FCSTD DOCUMENT  (FreeCAD 0.21R33771 (Git))
Label: jrobot-x-axis-assembly
License: All rights reserved
LicenseURL: http://en.wikipedia.org/wiki/All_rights_reserved
objects: App::Link×76, App::DocumentObjectGroup×3, PartDesign::CoordinateSystem×1, App::FeaturePython×1, Spreadsheet::Sheet×1, App::Part×1
note: 1 computed .brp shape members not serialized (recipe doc carries the construction recipe); baked Part::Feature solids carry a one-line shape summary decoded from their .brp
EXTERNAL_REF file=jrobot-x-axis-parts.FCStd obj=LCS_X_Axis_Base_Top
EXTERNAL_REF file=jrobot-x-axis-parts.FCStd obj=LCS_X_Axis_Top_Origin
EXTERNAL_REF file=jrobot-x-axis-parts.FCStd obj=Part
EXTERNAL_REF file=jrobot-x-axis-parts.FCStd obj=LCS_X_Axis_Top_Bearing_0
EXTERNAL_REF file=standard-parts.FCStd obj=LCS_Bearing_78mm_60mm_Bottom004
EXTERNAL_REF file=standard-parts.FCStd obj=Part006
EXTERNAL_REF file=jrobot-x-axis-parts.FCStd obj=LCS_X_Axis_Top_Bearing_1
EXTERNAL_REF file=standard-parts.FCStd obj=LCS_Bearing_78mm_60mm_Top004
EXTERNAL_REF file=jrobot-x-axis-parts.FCStd obj=LCS_X_Axis_Top_VerticalBearing_004
EXTERNAL_REF file=jrobot-x-axis-parts.FCStd obj=LCS_X_Axis_Top_VerticalBearing_2
EXTERNAL_REF file=jrobot-x-axis-parts.FCStd obj=LCS_X_Axis_Top_VerticalBearing_003
EXTERNAL_REF file=jrobot-x-axis-parts.FCStd obj=LCS_X_Axis_Top_VerticalBearing_3
EXTERNAL_REF file=jrobot-x-axis-parts.FCStd obj=LCS_X_Axis_Top_VerticalBearing_0
EXTERNAL_REF file=jrobot-x-axis-parts.FCStd obj=LCS_X_Axis_Top_LimitSwitch_0
EXTERNAL_REF file=standard-parts.FCStd obj=LCS_LimitSwitch_Hole0
EXTERNAL_REF file=standard-parts.FCStd obj=Part014
EXTERNAL_REF file=jrobot-x-axis-parts.FCStd obj=LCS_X_Axis_Base_BearingCap_To
EXTERNAL_REF file=jrobot-x-axis-parts.FCStd obj=Part018
EXTERNAL_REF file=jrobot-x-axis-parts.FCStd obj=LCS_X_Axis_Base_Origin
EXTERNAL_REF file=jrobot-x-axis-parts.FCStd obj=Part019
EXTERNAL_REF file=jrobot-x-axis-parts.FCStd obj=LCS_MotorMount_Origin
EXTERNAL_REF file=jrobot-x-axis-parts.FCStd obj=LCS_X_Axis_Top_MotorMount
EXTERNAL_REF file=jrobot-x-axis-parts.FCStd obj=Part020
EXTERNAL_REF file=jrobot-x-axis-parts.FCStd obj=LCS_X_Axis_MotorMount_Motor
EXTERNAL_REF file=standard-parts.FCStd obj=LCS_Nema23_76mm_MountFace
EXTERNAL_REF file=standard-parts.FCStd obj=Part015
EXTERNAL_REF file=jrobot-x-axis-parts.FCStd obj=LCS_X_Axis_Belt_Origin
EXTERNAL_REF file=jrobot-x-axis-parts.FCStd obj=LCS_X_Axis_Rotor_Belt
EXTERNAL_REF file=jrobot-x-axis-parts.FCStd obj=Part021
EXTERNAL_REF file=jrobot-x-axis-parts.FCStd obj=LCS_X_Axis_Rotor_Origin
EXTERNAL_REF file=jrobot-x-axis-parts.FCStd obj=LCS_X_Axis_Top_Rotor
EXTERNAL_REF file=jrobot-x-axis-parts.FCStd obj=Part022
EXTERNAL_REF file=jrobot-x-axis-parts.FCStd obj=LCS_X_Axis_BeltTensioner_Origin
EXTERNAL_REF file=jrobot-x-axis-parts.FCStd obj=LCS_X_Axis_MotorMount_Tensioner
EXTERNAL_REF file=jrobot-x-axis-parts.FCStd obj=Part023
EXTERNAL_REF file=jrobot-x-axis-parts.FCStd obj=LCS_X_Axis_BeltTensioner_Idler0
EXTERNAL_REF file=standard-parts.FCStd obj=LCS_Belt_Idler_GT2_10mm_Bottom
EXTERNAL_REF file=standard-parts.FCStd obj=Part009
EXTERNAL_REF file=jrobot-x-axis-parts.FCStd obj=LCS_X_Axis_BeltTensioner_Idler1
EXTERNAL_REF file=jrobot-x-axis-parts.FCStd obj=LCS_X_Axis_Shaft_Bottom
EXTERNAL_REF file=jrobot-x-axis-parts.FCStd obj=Part024
EXTERNAL_REF file=jrobot-x-axis-parts.FCStd obj=LCS_X_Axis_BeltTensioner_Bolt0
EXTERNAL_REF file=standard-parts.FCStd obj=LCS_M3_16_Screw
EXTERNAL_REF file=standard-parts.FCStd obj=Part020
EXTERNAL_REF file=jrobot-x-axis-parts.FCStd obj=LCS_X_Axis_BeltTensioner_Bolt1
EXTERNAL_REF file=standard-parts.FCStd obj=LCS_LimitSwitch_Hole0_Top
EXTERNAL_REF file=standard-parts.FCStd obj=LCS_M3_12_Screw
EXTERNAL_REF file=standard-parts.FCStd obj=Part018
EXTERNAL_REF file=standard-parts.FCStd obj=LCS_LimitSwitch_Hole1_Top
EXTERNAL_REF file=jrobot-x-axis-parts.FCStd obj=LCS_X_Axis_BeltTensioner_IdlerBolt0
EXTERNAL_REF file=standard-parts.FCStd obj=LCS_M5_25_Screw
EXTERNAL_REF file=standard-parts.FCStd obj=Part031
EXTERNAL_REF file=jrobot-x-axis-parts.FCStd obj=LCS_X_Axis_BeltTensioner_IdlerBolt1
EXTERNAL_REF file=standard-parts.FCStd obj=LCS_M3_Nut001
EXTERNAL_REF file=standard-parts.FCStd obj=Part037
EXTERNAL_REF file=standard-parts.FCStd obj=LCS_M5_20_Screw
EXTERNAL_REF file=standard-parts.FCStd obj=LCS_Nema23_76mm_Hole0
EXTERNAL_REF file=standard-parts.FCStd obj=Part030
EXTERNAL_REF file=standard-parts.FCStd obj=LCS_Nema23_76mm_Hole1
EXTERNAL_REF file=standard-parts.FCStd obj=LCS_Nema23_76mm_Hole2
EXTERNAL_REF file=standard-parts.FCStd obj=LCS_Nema23_76mm_Hole3
EXTERNAL_REF file=standard-parts.FCStd obj=LCS_Belt_Sprocket_GT2_6mm_5mm_Top001
EXTERNAL_REF file=standard-parts.FCStd obj=LCS_Nema23_76mm_Shaft
EXTERNAL_REF file=standard-parts.FCStd obj=Part038
EXTERNAL_REF file=jrobot-x-axis-parts.FCStd obj=LCS_X_Axis_Base_Bolt0
EXTERNAL_REF file=jrobot-x-axis-parts.FCStd obj=LCS_X_Axis_Base_Bolt1
EXTERNAL_REF file=jrobot-x-axis-parts.FCStd obj=LCS_X_Axis_Base_Bolt2
EXTERNAL_REF file=jrobot-x-axis-parts.FCStd obj=LCS_X_Axis_Base_Bolt3
EXTERNAL_REF file=jrobot-x-axis-parts.FCStd obj=LCS_X_Axis_Base_Bolt4
EXTERNAL_REF file=standard-parts.FCStd obj=LCS_M3_Nut
EXTERNAL_REF file=standard-parts.FCStd obj=Part024
EXTERNAL_REF file=jrobot-x-axis-parts.FCStd obj=LCS_X_Axis_Base_VerticalBearing_Bolt0
EXTERNAL_REF file=standard-parts.FCStd obj=LCS_M5_17_Screw
EXTERNAL_REF file=standard-parts.FCStd obj=Part029
EXTERNAL_REF file=jrobot-x-axis-parts.FCStd obj=LCS_X_Axis_Base_VerticalBearing_Bolt1
EXTERNAL_REF file=jrobot-x-axis-parts.FCStd obj=LCS_X_Axis_Base_VerticalBearing_Bolt2
EXTERNAL_REF file=jrobot-x-axis-parts.FCStd obj=LCS_X_Axis_Base_VerticalBearing_Bolt3
EXTERNAL_REF file=jrobot-x-axis-parts.FCStd obj=LCS_X_Axis_Base_VerticalBearing_Bolt4
EXTERNAL_REF file=jrobot-x-axis-parts.FCStd obj=LCS_X_Axis_Top_LimitSwitch_1
EXTERNAL_REF file=jrobot-x-axis-parts.FCStd obj=LCS_X_Axis_Base_Mount0
EXTERNAL_REF file=standard-parts.FCStd obj=LCS_M5_45_Screw001
EXTERNAL_REF file=standard-parts.FCStd obj=Part032
EXTERNAL_REF file=jrobot-x-axis-parts.FCStd obj=LCS_X_Axis_Base_Mount1
EXTERNAL_REF file=standard-parts.FCStd obj=LCS_M5_30_Screw
EXTERNAL_REF file=jrobot-x-axis-parts.FCStd obj=LCS_X_Axis_Base_Mount2
EXTERNAL_REF file=jrobot-x-axis-parts.FCStd obj=LCS_X_Axis_Base_Mount3
EXTERNAL_REF file=jrobot-x-axis-parts.FCStd obj=LCS_X_Axis_MotorMount_Mount0
EXTERNAL_REF file=jrobot-x-axis-parts.FCStd obj=LCS_X_Axis_MotorMount_Mount1
EXTERNAL_REF file=jrobot-x-axis-parts.FCStd obj=LCS_X_Axis_MotorMount_Mount2
EXTERNAL_REF file=jrobot-x-axis-parts.FCStd obj=LCS_X_Axis_MotorMount_Mount3

FEATURE [PartDesign::CoordinateSystem] LCS_Origin
  AttacherType = Attacher::AttachEngine3D
  MapMode = 2
  Support = -> [X_Axis]
FEATURE [App::DocumentObjectGroup] Constraints
FEATURE [App::FeaturePython] Variables  # WARN: FeaturePython — macro-defined, semantics opaque (R4)
  Type = App::PropertyContainer
FEATURE [App::DocumentObjectGroup] Configurations
FEATURE [App::Link] P_X_Axis_Top
  AttachedBy = #LCS_X_Axis_Top_Origin
  AttachedTo = P_X_Axis_Base#LCS_X_Axis_Base_Top
  LinkPlacement = pos=(0,0,42) rot=(0,0,1;0rad)
  LinkedObject = -> <external jrobot-x-axis-parts.FCStd>#Part
  Placement = pos=(0,0,42) rot=(0,0,1;0rad)
  SolverId = Asm4EE
  expr: Placement = P_X_Axis_Base.Placement * jrobot_x_axis_parts#LCS_X_Axis_Base_Top.Placement * AttachmentOffset * jrobot_x_axis_parts#LCS_X_Axis_Top_Origin.Placement ^ -1
FEATURE [App::Link] P_Bearing_5mm_16mm_5mm  label="P_Bearing_5mm_16mm_5mm_axis_bottom"
  AttachedBy = #LCS_Bearing_78mm_60mm_Bottom004
  AttachedTo = P_X_Axis_Top#LCS_X_Axis_Top_Bearing_0
  AttachmentOffset = pos=(0,0,0) rot=(1,0,0;3.14159rad)
  LinkPlacement = pos=(0,0,47) rot=(0.707107,0.707107,0;3.14159rad)
  LinkedObject = -> <external standard-parts.FCStd>#Part006
  Placement = pos=(0,0,47) rot=(0.707107,0.707107,0;3.14159rad)
  SolverId = Asm4EE
  expr: Placement = P_X_Axis_Top.Placement * jrobot_x_axis_parts#LCS_X_Axis_Top_Bearing_0.Placement * AttachmentOffset * standard_parts#LCS_Bearing_78mm_60mm_Bottom004.Placement ^ -1
FEATURE [App::Link] P_Bearing_5mm_16mm_5mm001  label="P_Bearing_5mm_16mm_5mm_axis_top"
  AttachedBy = #LCS_Bearing_78mm_60mm_Top004
  AttachedTo = P_X_Axis_Top#LCS_X_Axis_Top_Bearing_1
  AttachmentOffset = pos=(0,0,0) rot=(1,0,0;3.14159rad)
  LinkPlacement = pos=(-6e-16,0,82) rot=(0.707107,0.707107,0;3.14159rad)
  LinkedObject = -> <external standard-parts.FCStd>#Part006
  Placement = pos=(-6e-16,0,82) rot=(0.707107,0.707107,0;3.14159rad)
  SolverId = Asm4EE
  expr: Placement = P_X_Axis_Top.Placement * jrobot_x_axis_parts#LCS_X_Axis_Top_Bearing_1.Placement * AttachmentOffset * standard_parts#LCS_Bearing_78mm_60mm_Top004.Placement ^ -1
FEATURE [App::Link] P_Bearing_5mm_16mm_1  label="P_Bearing_5mm_16mm_radial_1"
  AttachedBy = #LCS_Bearing_78mm_60mm_Bottom004
  AttachedTo = P_X_Axis_Top#LCS_X_Axis_Top_VerticalBearing_004
  LinkPlacement = pos=(-77.5,2.49e-14,77) rot=(0.707107,0,-0.707107;3.14159rad)
  LinkedObject = -> <external standard-parts.FCStd>#Part006
  Placement = pos=(-77.5,2.49e-14,77) rot=(0.707107,0,-0.707107;3.14159rad)
  SolverId = Asm4EE
  expr: Placement = P_X_Axis_Top.Placement * jrobot_x_axis_parts#LCS_X_Axis_Top_VerticalBearing_004.Placement * AttachmentOffset * standard_parts#LCS_Bearing_78mm_60mm_Bottom004.Placement ^ -1
FEATURE [App::Link] P_Bearing_5mm_16mm_2  label="P_Bearing_5mm_16mm_radial_2"
  AttachedBy = #LCS_Bearing_78mm_60mm_Bottom004
  AttachedTo = P_X_Axis_Top#LCS_X_Axis_Top_VerticalBearing_2
  LinkPlacement = pos=(-23.9488,-73.7069,77) rot=(0.62896,0.456966,-0.62896;2.28433rad)
  LinkedObject = -> <external standard-parts.FCStd>#Part006
  Placement = pos=(-23.9488,-73.7069,77) rot=(0.62896,0.456966,-0.62896;2.28433rad)
  SolverId = Asm4EE
  expr: Placement = P_X_Axis_Top.Placement * jrobot_x_axis_parts#LCS_X_Axis_Top_VerticalBearing_2.Placement * AttachmentOffset * standard_parts#LCS_Bearing_78mm_60mm_Bottom004.Placement ^ -1
FEATURE [App::Link] P_Bearing_5mm_16mm_3  label="P_Bearing_5mm_16mm_radial_3"
  AttachedBy = #LCS_Bearing_78mm_60mm_Bottom004
  AttachedTo = P_X_Axis_Top#LCS_X_Axis_Top_VerticalBearing_003
  LinkPlacement = pos=(62.6988,-45.5534,77) rot=(0.295242,0.908661,-0.295242;1.66643rad)
  LinkedObject = -> <external standard-parts.FCStd>#Part006
  Placement = pos=(62.6988,-45.5534,77) rot=(0.295242,0.908661,-0.295242;1.66643rad)
  SolverId = Asm4EE
  expr: Placement = P_X_Axis_Top.Placement * jrobot_x_axis_parts#LCS_X_Axis_Top_VerticalBearing_003.Placement * AttachmentOffset * standard_parts#LCS_Bearing_78mm_60mm_Bottom004.Placement ^ -1
FEATURE [App::Link] P_Bearing_5mm_16mm_4  label="P_Bearing_5mm_16mm_radial_4"
  AttachedBy = #LCS_Bearing_78mm_60mm_Bottom004
  AttachedTo = P_X_Axis_Top#LCS_X_Axis_Top_VerticalBearing_3
  LinkPlacement = pos=(62.6988,45.5534,77) rot=(-0.295242,0.908661,0.295242;1.66643rad)
  LinkedObject = -> <external standard-parts.FCStd>#Part006
  Placement = pos=(62.6988,45.5534,77) rot=(-0.295242,0.908661,0.295242;1.66643rad)
  SolverId = Asm4EE
  expr: Placement = P_X_Axis_Top.Placement * jrobot_x_axis_parts#LCS_X_Axis_Top_VerticalBearing_3.Placement * AttachmentOffset * standard_parts#LCS_Bearing_78mm_60mm_Bottom004.Placement ^ -1
FEATURE [App::Link] P_Bearing_5mm_16mm_5mm002  label="P_Bearing_5mm_16mm_radial_0"
  AttachedBy = #LCS_Bearing_78mm_60mm_Bottom004
  AttachedTo = P_X_Axis_Top#LCS_X_Axis_Top_VerticalBearing_0
  LinkPlacement = pos=(-23.9488,73.7069,77) rot=(0.111299,-0.702714,-0.702714;2.91991rad)
  LinkedObject = -> <external standard-parts.FCStd>#Part006
  Placement = pos=(-23.9488,73.7069,77) rot=(0.111299,-0.702714,-0.702714;2.91991rad)
  SolverId = Asm4EE
  expr: Placement = P_X_Axis_Top.Placement * jrobot_x_axis_parts#LCS_X_Axis_Top_VerticalBearing_0.Placement * AttachmentOffset * standard_parts#LCS_Bearing_78mm_60mm_Bottom004.Placement ^ -1
FEATURE [App::Link] P_LimitSwitch
  AttachedBy = #LCS_LimitSwitch_Hole0
  AttachedTo = P_X_Axis_Top#LCS_X_Axis_Top_LimitSwitch_0
  AttachmentOffset = pos=(0,0,0) rot=(0,0,-1;3.14159rad)
  LinkPlacement = pos=(6.875,55.8,82) rot=(0,0,-1;3.14159rad)
  LinkedObject = -> <external standard-parts.FCStd>#Part014
  Placement = pos=(6.875,55.8,82) rot=(0,0,-1;3.14159rad)
  SolverId = Asm4EE
  expr: Placement = P_X_Axis_Top.Placement * jrobot_x_axis_parts#LCS_X_Axis_Top_LimitSwitch_0.Placement * AttachmentOffset * standard_parts#LCS_LimitSwitch_Hole0.Placement ^ -1
FEATURE [App::Link] P_Robot_X_Axis_Base_BearingCap
  AttachedBy = #LCS_X_Axis_Base_BearingCap_To
  AttachedTo = P_X_Axis_Top#LCS_X_Axis_Top_Origin
  LinkPlacement = pos=(0,0,40) rot=(0,0,1;0rad)
  LinkedObject = -> <external jrobot-x-axis-parts.FCStd>#Part018
  Placement = pos=(0,0,40) rot=(0,0,1;0rad)
  SolverId = Asm4EE
  expr: Placement = P_X_Axis_Top.Placement * jrobot_x_axis_parts#LCS_X_Axis_Top_Origin.Placement * AttachmentOffset * jrobot_x_axis_parts#LCS_X_Axis_Base_BearingCap_To.Placement ^ -1
FEATURE [App::Link] P_X_Axis_Base
  AttachedBy = #LCS_X_Axis_Base_Origin
  AttachedTo = Parent Assembly#LCS_Origin
  LinkedObject = -> <external jrobot-x-axis-parts.FCStd>#Part019
  SolverId = Asm4EE
  expr: Placement = LCS_Origin.Placement * AttachmentOffset * jrobot_x_axis_parts#LCS_X_Axis_Base_Origin.Placement ^ -1
FEATURE [App::Link] P_X_Axis_MotorMount
  AttachedBy = #LCS_MotorMount_Origin
  AttachedTo = P_X_Axis_Top#LCS_X_Axis_Top_MotorMount
  AttachmentOffset = pos=(0,0,0) rot=(0,0,1;3.14159rad)
  LinkPlacement = pos=(-1.1e-14,0,80) rot=(0,0,1;3.14159rad)
  LinkedObject = -> <external jrobot-x-axis-parts.FCStd>#Part020
  Placement = pos=(-1.1e-14,0,80) rot=(0,0,1;3.14159rad)
  SolverId = Asm4EE
  expr: Placement = P_X_Axis_Top.Placement * jrobot_x_axis_parts#LCS_X_Axis_Top_MotorMount.Placement * AttachmentOffset * jrobot_x_axis_parts#LCS_MotorMount_Origin.Placement ^ -1
FEATURE [App::Link] P_Nema23_76mm
  AttachedBy = #LCS_Nema23_76mm_MountFace
  AttachedTo = P_X_Axis_MotorMount#LCS_X_Axis_MotorMount_Motor
  LinkPlacement = pos=(4.1e-15,123.5,2) rot=(0,0,1;3.14159rad)
  LinkedObject = -> <external standard-parts.FCStd>#Part015
  Placement = pos=(4.1e-15,123.5,2) rot=(0,0,1;3.14159rad)
  SolverId = Asm4EE
  expr: Placement = P_X_Axis_MotorMount.Placement * jrobot_x_axis_parts#LCS_X_Axis_MotorMount_Motor.Placement * AttachmentOffset * standard_parts#LCS_Nema23_76mm_MountFace.Placement ^ -1
FEATURE [App::Link] P_X_Axis_Belt
  AttachedBy = #LCS_X_Axis_Belt_Origin
  AttachedTo = P_X_Axis_Rotor#LCS_X_Axis_Rotor_Belt
  LinkPlacement = pos=(0,0,87) rot=(0,0,1;0rad)
  LinkedObject = -> <external jrobot-x-axis-parts.FCStd>#Part021
  Placement = pos=(0,0,87) rot=(0,0,1;0rad)
  SolverId = Asm4EE
  expr: Placement = P_X_Axis_Rotor.Placement * jrobot_x_axis_parts#LCS_X_Axis_Rotor_Belt.Placement * AttachmentOffset * jrobot_x_axis_parts#LCS_X_Axis_Belt_Origin.Placement ^ -1
FEATURE [App::Link] P_X_Axis_Rotor
  AttachedBy = #LCS_X_Axis_Rotor_Origin
  AttachedTo = P_X_Axis_Top#LCS_X_Axis_Top_Rotor
  LinkPlacement = pos=(0,0,85) rot=(0,0,1;0rad)
  LinkedObject = -> <external jrobot-x-axis-parts.FCStd>#Part022
  Placement = pos=(0,0,85) rot=(0,0,1;0rad)
  SolverId = Asm4EE
  expr: Placement = P_X_Axis_Top.Placement * jrobot_x_axis_parts#LCS_X_Axis_Top_Rotor.Placement * AttachmentOffset * jrobot_x_axis_parts#LCS_X_Axis_Rotor_Origin.Placement ^ -1
FEATURE [App::Link] P_X_Axis_BeltTensioner
  AttachedBy = #LCS_X_Axis_BeltTensioner_Origin
  AttachedTo = P_X_Axis_MotorMount#LCS_X_Axis_MotorMount_Tensioner
  LinkPlacement = pos=(4.1e-15,123.5,85) rot=(0,0,1;3.14159rad)
  LinkedObject = -> <external jrobot-x-axis-parts.FCStd>#Part023
  Placement = pos=(4.1e-15,123.5,85) rot=(0,0,1;3.14159rad)
  SolverId = Asm4EE
  expr: Placement = P_X_Axis_MotorMount.Placement * jrobot_x_axis_parts#LCS_X_Axis_MotorMount_Tensioner.Placement * AttachmentOffset * jrobot_x_axis_parts#LCS_X_Axis_BeltTensioner_Origin.Placement ^ -1
FEATURE [App::Link] P_Belt_Idler_GT2_10mm_5mm
  AttachedBy = #LCS_Belt_Idler_GT2_10mm_Bottom
  AttachedTo = P_X_Axis_BeltTensioner#LCS_X_Axis_BeltTensioner_Idler0
  AttachmentOffset = pos=(0,0,1) rot=(0,0,1;0rad)
  LinkPlacement = pos=(15,116,98.5) rot=(-0.707107,0.707107,0;3.14159rad)
  LinkedObject = -> <external standard-parts.FCStd>#Part009
  Placement = pos=(15,116,98.5) rot=(-0.707107,0.707107,0;3.14159rad)
  SolverId = Asm4EE
  expr: Placement = P_X_Axis_BeltTensioner.Placement * jrobot_x_axis_parts#LCS_X_Axis_BeltTensioner_Idler0.Placement * AttachmentOffset * standard_parts#LCS_Belt_Idler_GT2_10mm_Bottom.Placement ^ -1
FEATURE [App::Link] P_Belt_Idler_GT2_10mm_5mm_2
  AttachedBy = #LCS_Belt_Idler_GT2_10mm_Bottom
  AttachedTo = P_X_Axis_BeltTensioner#LCS_X_Axis_BeltTensioner_Idler1
  AttachmentOffset = pos=(0,0,1) rot=(0,0,1;0rad)
  LinkPlacement = pos=(-15,116,98.5) rot=(-0.707107,0.707107,0;3.14159rad)
  LinkedObject = -> <external standard-parts.FCStd>#Part009
  Placement = pos=(-15,116,98.5) rot=(-0.707107,0.707107,0;3.14159rad)
  SolverId = Asm4EE
  expr: Placement = P_X_Axis_BeltTensioner.Placement * jrobot_x_axis_parts#LCS_X_Axis_BeltTensioner_Idler1.Placement * AttachmentOffset * standard_parts#LCS_Belt_Idler_GT2_10mm_Bottom.Placement ^ -1
FEATURE [App::Link] P_X_Axis_Shaft
  AttachedBy = #LCS_X_Axis_Shaft_Bottom
  AttachedTo = P_Robot_X_Axis_Base_BearingCap#LCS_X_Axis_Base_BearingCap_To
  LinkPlacement = pos=(0,0,42) rot=(0,0,1;0rad)
  LinkedObject = -> <external jrobot-x-axis-parts.FCStd>#Part024
  Placement = pos=(0,0,42) rot=(0,0,1;0rad)
  SolverId = Asm4EE
  expr: Placement = P_Robot_X_Axis_Base_BearingCap.Placement * jrobot_x_axis_parts#LCS_X_Axis_Base_BearingCap_To.Placement * AttachmentOffset * jrobot_x_axis_parts#LCS_X_Axis_Shaft_Bottom.Placement ^ -1
FEATURE [App::Link] P_M3_16_Screw  label="P_X_Axis_BeltTensioner_Bolt0_Bolt"
  AttachedBy = #LCS_M3_16_Screw
  AttachedTo = P_X_Axis_BeltTensioner#LCS_X_Axis_BeltTensioner_Bolt0
  LinkPlacement = pos=(42.5,123.5,83) rot=(0,0,1;4.71239rad)
  LinkedObject = -> <external standard-parts.FCStd>#Part020
  Placement = pos=(42.5,123.5,83) rot=(0,0,1;4.71239rad)
  SolverId = Asm4EE
  expr: Placement = P_X_Axis_BeltTensioner.Placement * jrobot_x_axis_parts#LCS_X_Axis_BeltTensioner_Bolt0.Placement * AttachmentOffset * standard_parts#LCS_M3_16_Screw.Placement ^ -1
FEATURE [App::Link] X_Axis_BeltTensioner_Bolt0_Screw  label="P_X_Axis_BeltTensioner_Bolt1_Bolt"
  AttachedBy = #LCS_M3_16_Screw
  AttachedTo = P_X_Axis_BeltTensioner#LCS_X_Axis_BeltTensioner_Bolt1
  LinkPlacement = pos=(-42.5,123.5,83) rot=(0,0,1;4.71239rad)
  LinkedObject = -> <external standard-parts.FCStd>#Part020
  Placement = pos=(-42.5,123.5,83) rot=(0,0,1;4.71239rad)
  SolverId = Asm4EE
  expr: Placement = P_X_Axis_BeltTensioner.Placement * jrobot_x_axis_parts#LCS_X_Axis_BeltTensioner_Bolt1.Placement * AttachmentOffset * standard_parts#LCS_M3_16_Screw.Placement ^ -1
FEATURE [App::Link] P_M3_12_Screw  label="P_X_Axis_LimitSwitch_Hole0_Bolt"
  AttachedBy = #LCS_M3_12_Screw
  AttachedTo = P_LimitSwitch#LCS_LimitSwitch_Hole0_Top
  LinkPlacement = pos=(9.625,50,84) rot=(0,0,-1;1.5708rad)
  LinkedObject = -> <external standard-parts.FCStd>#Part018
  Placement = pos=(9.625,50,84) rot=(0,0,-1;1.5708rad)
  SolverId = Asm4EE
  expr: Placement = P_LimitSwitch.Placement * standard_parts#LCS_LimitSwitch_Hole0_Top.Placement * AttachmentOffset * standard_parts#LCS_M3_12_Screw.Placement ^ -1
FEATURE [App::Link] P_M3_12_Screw_2  label="P_X_Axis_LimitSwitch_Hole1_Bolt"
  AttachedBy = #LCS_M3_12_Screw
  AttachedTo = P_LimitSwitch#LCS_LimitSwitch_Hole1_Top
  LinkPlacement = pos=(-9.625,50,84) rot=(0,0,-1;1.5708rad)
  LinkedObject = -> <external standard-parts.FCStd>#Part018
  Placement = pos=(-9.625,50,84) rot=(0,0,-1;1.5708rad)
  SolverId = Asm4EE
  expr: Placement = P_LimitSwitch.Placement * standard_parts#LCS_LimitSwitch_Hole1_Top.Placement * AttachmentOffset * standard_parts#LCS_M3_12_Screw.Placement ^ -1
FEATURE [App::Link] P_M5_25_Screw  label="P_X_Axis_BeltTensioner_IdlerBolt0_Bolt"
  AttachedBy = #LCS_M5_25_Screw
  AttachedTo = P_X_Axis_BeltTensioner#LCS_X_Axis_BeltTensioner_IdlerBolt0
  LinkPlacement = pos=(15,116,111) rot=(0,0,1;4.71239rad)
  LinkedObject = -> <external standard-parts.FCStd>#Part031
  Placement = pos=(15,116,111) rot=(0,0,1;4.71239rad)
  SolverId = Asm4EE
  expr: Placement = P_X_Axis_BeltTensioner.Placement * jrobot_x_axis_parts#LCS_X_Axis_BeltTensioner_IdlerBolt0.Placement * AttachmentOffset * standard_parts#LCS_M5_25_Screw.Placement ^ -1
FEATURE [App::Link] P_M5_25_Screw_2  label="P_X_Axis_BeltTensioner_IdlerBolt1_Bolt"
  AttachedBy = #LCS_M5_25_Screw
  AttachedTo = P_X_Axis_BeltTensioner#LCS_X_Axis_BeltTensioner_IdlerBolt1
  LinkPlacement = pos=(-15,116,111) rot=(0,0,1;4.71239rad)
  LinkedObject = -> <external standard-parts.FCStd>#Part031
  Placement = pos=(-15,116,111) rot=(0,0,1;4.71239rad)
  SolverId = Asm4EE
  expr: Placement = P_X_Axis_BeltTensioner.Placement * jrobot_x_axis_parts#LCS_X_Axis_BeltTensioner_IdlerBolt1.Placement * AttachmentOffset * standard_parts#LCS_M5_25_Screw.Placement ^ -1
FEATURE [App::Link] P_M5_Nut  label="P_X_Axis_BeltTensioner_IdlerBolt0_Nut"
  AttachedBy = #LCS_M3_Nut001
  AttachedTo = P_X_Axis_BeltTensioner#LCS_X_Axis_BeltTensioner_IdlerBolt0
  AttachmentOffset = pos=(0,0,-9.5) rot=(0,0,1;0rad)
  LinkPlacement = pos=(15,116,101.5) rot=(0,0,1;4.71239rad)
  LinkedObject = -> <external standard-parts.FCStd>#Part037
  Placement = pos=(15,116,101.5) rot=(0,0,1;4.71239rad)
  SolverId = Asm4EE
  expr: Placement = P_X_Axis_BeltTensioner.Placement * jrobot_x_axis_parts#LCS_X_Axis_BeltTensioner_IdlerBolt0.Placement * AttachmentOffset * standard_parts#LCS_M3_Nut001.Placement ^ -1
FEATURE [App::Link] P_M5_Nut001  label="P_X_Axis_BeltTensioner_IdlerBolt1_Nut"
  AttachedBy = #LCS_M3_Nut001
  AttachedTo = P_X_Axis_BeltTensioner#LCS_X_Axis_BeltTensioner_IdlerBolt1
  AttachmentOffset = pos=(0,0,-9.5) rot=(0,0,1;0rad)
  LinkPlacement = pos=(-15,116,101.5) rot=(0,0,1;4.71239rad)
  LinkedObject = -> <external standard-parts.FCStd>#Part037
  Placement = pos=(-15,116,101.5) rot=(0,0,1;4.71239rad)
  SolverId = Asm4EE
  expr: Placement = P_X_Axis_BeltTensioner.Placement * jrobot_x_axis_parts#LCS_X_Axis_BeltTensioner_IdlerBolt1.Placement * AttachmentOffset * standard_parts#LCS_M3_Nut001.Placement ^ -1
FEATURE [App::Link] P_M5_20_Screw  label="P_X_Axis_Nema17_Bolt0_Bolt"
  AttachedBy = #LCS_M5_20_Screw
  AttachedTo = P_Nema23_76mm#LCS_Nema23_76mm_Hole0
  AttachmentOffset = pos=(0,0,2) rot=(0,0,1;0rad)
  LinkPlacement = pos=(-23.5,100,80) rot=(0,0,1;3.14159rad)
  LinkedObject = -> <external standard-parts.FCStd>#Part030
  Placement = pos=(-23.5,100,80) rot=(0,0,1;3.14159rad)
  SolverId = Asm4EE
  expr: Placement = P_Nema23_76mm.Placement * standard_parts#LCS_Nema23_76mm_Hole0.Placement * AttachmentOffset * standard_parts#LCS_M5_20_Screw.Placement ^ -1
FEATURE [App::Link] P_M5_20_Screw001  label="P_X_Axis_Nema17_Bolt1_Bolt"
  AttachedBy = #LCS_M5_20_Screw
  AttachedTo = P_Nema23_76mm#LCS_Nema23_76mm_Hole1
  AttachmentOffset = pos=(0,0,2) rot=(0,0,1;0rad)
  LinkPlacement = pos=(23.5,100,80) rot=(0,0,1;3.14159rad)
  LinkedObject = -> <external standard-parts.FCStd>#Part030
  Placement = pos=(23.5,100,80) rot=(0,0,1;3.14159rad)
  SolverId = Asm4EE
  expr: Placement = P_Nema23_76mm.Placement * standard_parts#LCS_Nema23_76mm_Hole1.Placement * AttachmentOffset * standard_parts#LCS_M5_20_Screw.Placement ^ -1
FEATURE [App::Link] P_X_Axis_Nema17_Bolt1_Screw  label="P_X_Axis_Nema17_Bolt2_Bolt"
  AttachedBy = #LCS_M5_20_Screw
  AttachedTo = P_Nema23_76mm#LCS_Nema23_76mm_Hole2
  AttachmentOffset = pos=(0,0,2) rot=(0,0,1;0rad)
  LinkPlacement = pos=(-23.5,147,80) rot=(0,0,1;3.14159rad)
  LinkedObject = -> <external standard-parts.FCStd>#Part030
  Placement = pos=(-23.5,147,80) rot=(0,0,1;3.14159rad)
  SolverId = Asm4EE
  expr: Placement = P_Nema23_76mm.Placement * standard_parts#LCS_Nema23_76mm_Hole2.Placement * AttachmentOffset * standard_parts#LCS_M5_20_Screw.Placement ^ -1
FEATURE [App::Link] P_X_Axis_Nema17_Bolt1_1  label="P_X_Axis_Nema17_Bolt3_Bolt"
  AttachedBy = #LCS_M5_20_Screw
  AttachedTo = P_Nema23_76mm#LCS_Nema23_76mm_Hole3
  AttachmentOffset = pos=(0,0,2) rot=(0,0,1;0rad)
  LinkPlacement = pos=(23.5,147,80) rot=(0,0,1;3.14159rad)
  LinkedObject = -> <external standard-parts.FCStd>#Part030
  Placement = pos=(23.5,147,80) rot=(0,0,1;3.14159rad)
  SolverId = Asm4EE
  expr: Placement = P_Nema23_76mm.Placement * standard_parts#LCS_Nema23_76mm_Hole3.Placement * AttachmentOffset * standard_parts#LCS_M5_20_Screw.Placement ^ -1
FEATURE [App::Link] P_M5_Nut002  label="P_X_Axis_Nema17_Nut0"
  AttachedBy = #LCS_M3_Nut001
  AttachedTo = P_Nema23_76mm#LCS_Nema23_76mm_Hole0
  AttachmentOffset = pos=(0,0,-10) rot=(0,0,1;0rad)
  LinkPlacement = pos=(-23.5,100,68) rot=(0,0,1;3.14159rad)
  LinkedObject = -> <external standard-parts.FCStd>#Part037
  Placement = pos=(-23.5,100,68) rot=(0,0,1;3.14159rad)
  SolverId = Asm4EE
  expr: Placement = P_Nema23_76mm.Placement * standard_parts#LCS_Nema23_76mm_Hole0.Placement * AttachmentOffset * standard_parts#LCS_M3_Nut001.Placement ^ -1
FEATURE [App::Link] P_M5_Nut_2  label="P_X_Axis_Nema17_Nut1"
  AttachedBy = #LCS_M3_Nut001
  AttachedTo = P_Nema23_76mm#LCS_Nema23_76mm_Hole1
  AttachmentOffset = pos=(0,0,-10) rot=(0,0,1;0rad)
  LinkPlacement = pos=(23.5,100,68) rot=(0,0,1;3.14159rad)
  LinkedObject = -> <external standard-parts.FCStd>#Part037
  Placement = pos=(23.5,100,68) rot=(0,0,1;3.14159rad)
  SolverId = Asm4EE
  expr: Placement = P_Nema23_76mm.Placement * standard_parts#LCS_Nema23_76mm_Hole1.Placement * AttachmentOffset * standard_parts#LCS_M3_Nut001.Placement ^ -1
FEATURE [App::Link] P_M5_Nut_1  label="P_X_Axis_Nema17_Nut2"
  AttachedBy = #LCS_M3_Nut001
  AttachedTo = P_Nema23_76mm#LCS_Nema23_76mm_Hole2
  AttachmentOffset = pos=(0,0,-10) rot=(0,0,1;0rad)
  LinkPlacement = pos=(-23.5,147,68) rot=(0,0,1;3.14159rad)
  LinkedObject = -> <external standard-parts.FCStd>#Part037
  Placement = pos=(-23.5,147,68) rot=(0,0,1;3.14159rad)
  SolverId = Asm4EE
  expr: Placement = P_Nema23_76mm.Placement * standard_parts#LCS_Nema23_76mm_Hole2.Placement * AttachmentOffset * standard_parts#LCS_M3_Nut001.Placement ^ -1
FEATURE [App::Link] P_M5_Nut003  label="P_X_Axis_Nema17_Nut3"
  AttachedBy = #LCS_M3_Nut001
  AttachedTo = P_Nema23_76mm#LCS_Nema23_76mm_Hole3
  AttachmentOffset = pos=(0,0,-10) rot=(0,0,1;0rad)
  LinkPlacement = pos=(23.5,147,68) rot=(0,0,1;3.14159rad)
  LinkedObject = -> <external standard-parts.FCStd>#Part037
  Placement = pos=(23.5,147,68) rot=(0,0,1;3.14159rad)
  SolverId = Asm4EE
  expr: Placement = P_Nema23_76mm.Placement * standard_parts#LCS_Nema23_76mm_Hole3.Placement * AttachmentOffset * standard_parts#LCS_M3_Nut001.Placement ^ -1
FEATURE [App::Link] P_Belt_Sprocket_GT2_6mm_10mm
  AttachedBy = #LCS_Belt_Sprocket_GT2_6mm_5mm_Top001
  AttachedTo = P_Nema23_76mm#LCS_Nema23_76mm_Shaft
  LinkPlacement = pos=(4.1e-15,123.5,86) rot=(0,0,1;3.14159rad)
  LinkedObject = -> <external standard-parts.FCStd>#Part038
  Placement = pos=(4.1e-15,123.5,86) rot=(0,0,1;3.14159rad)
  SolverId = Asm4EE
  expr: Placement = P_Nema23_76mm.Placement * standard_parts#LCS_Nema23_76mm_Shaft.Placement * AttachmentOffset * standard_parts#LCS_Belt_Sprocket_GT2_6mm_5mm_Top001.Placement ^ -1
FEATURE [Spreadsheet::Sheet] BOM
  cells = A1='BomKey; B1='DrawingName; C1='DrawingRevision; D1='PartID; E1='PartDescription; F1='FileName; G1='FastenerDiameter; H1='FastenerLength; I1='FastenerType; J1='Qty.; A2='jrobot_x_axis_assembly#Assembly; B2='jrobot-x-axis-assembly.FCStd; D2='jrobot-x-axis-assembly; G2='-; H2='-; I2='-; J2=1; A3='jrobot_x_axis_parts#Part; B3='jrobot-x-axis-parts.FCStd; D3='jrobot-x-axis-parts; E3='B_X_Axis_Top; G3='-; H3='-; I3='-; J3=1; A4='standard_parts#Part006; B4='standard-parts.FCStd; D4='standard-parts; E4='B_Bearing_5mm_16mm_5mm; G4='-; H4='-; I4='-; J4=7; A5='jrobot_x_axis_parts#Part019; B5='jrobot-x-axis-parts.FCStd; D5='jrobot-x-axis-parts; E5='B_X_Axis_Base; G5='-; H5='-; I5='-; J5=1; A6='jrobot_x_axis_parts#Part018; B6='jrobot-x-axis-parts.FCStd; D6='jrobot-x-axis-parts; E6='B_X_Axis_BearingCap; G6='-; H6='-; I6='-; J6=1; A7='standard_parts#Part014; B7='standard-parts.FCStd; D7='standard-parts; E7='B_LimitSwitch; G7='-; H7='-; I7='-; J7=1; A8='jrobot_x_axis_parts#Part020; B8='jrobot-x-axis-parts.FCStd; D8='jrobot-x-axis-parts; E8='B_X_Axis_MotorMount; G8='-; H8='-; I8='-; J8=1; A9='standard_parts#Part015; B9='standard-parts.FCStd; D9='standard-parts; E9='B_Nema23_76mm; G9='-; H9='-; I9='-; J9=1; A10='jrobot_x_axis_parts#Part021; B10='jrobot-x-axis-parts.FCStd; D10='jrobot-x-axis-parts; E10='B_X_Axis_Belt; G10='-; H10='-; I10='-; J10=1; A11='jrobot_x_axis_parts#Part022; B11='jrobot-x-axis-parts.FCStd; D11='jrobot-x-axis-parts; E11='B_X_Axis_Rotor; G11='-; H11='-; I11='-; J11=1; A12='jrobot_x_axis_parts#Part023; B12='jrobot-x-axis-parts.FCStd; D12='jrobot-x-axis-parts; E12='B_X_Axis_BeltTensioner; G12='-; H12='-; I12='-; J12=1; A13='standard_parts#Part009; B13='standard-parts.FCStd; D13='standard-parts; E13='B_Belt_Idler_GT2_10mm_5mm; G13='-; H13='-; I13='-; J13=2; A14='jrobot_x_axis_parts#Part024; B14='jrobot-x-axis-parts.FCStd; D14='jrobot-x-axis-parts; E14='B_X_Axis_Shaft; G14='-; H14='-; I14='-; J14=1; A15='standard_parts#Part020; B15='standard-parts.FCStd; D15='standard-parts; E15='B_M3_16_Screw; G15='-; H15='-; I15='-; J15=2; A16='M3x16-Screw(ISO4762); B16='All; C16='-; D16='M3x16-Screw(ISO4762); E16='-; F16='-; G16='M3; H16=16; I16='ISO4762; J16=2; A17='standard_parts#Part018; B17='standard-parts.FCStd; C17='a; D17='standard-parts; E17='B_M3_12_Screw; F17='a; G17='-; H17='-; I17='-; J17=2; A18='M3x12-Screw(ISO4762); B18='All; C18='-; D18='M3x12-Screw(ISO4762); E18='-; F18='-; G18='M3; H18=12; I18='ISO4762; J18=2; A19='standard_parts#Part031; B19='standard-parts.FCStd; D19='standard-parts; E19='B_M5_25_Screw; G19='-; H19='-; I19='-; J19=2; A20='M5x25-Screw(ISO4762); B20='All; C20='-; D20='M5x25-Screw(ISO4762); E20='-; F20='-; G20='M5; H20=25; I20='ISO4762; J20=2; A21='standard_parts#Part037; B21='standard-parts.FCStd; D21='standard-parts; E21='B_M5_Nut; G21='-; H21='-; I21='-; J21=6; A22='M5-Nut(ISO4032); B22='All; C22='-; D22='M5-Nut(ISO4032); E22='-; F22='-; G22='M5; I22='ISO4032; J22=6; A23='standard_parts#Part030; B23='standard-parts.FCStd; D23='standard-parts; E23='B_M5_20_Screw; G23='-; H23='-; I23='-; J23=4; A24='M5x20-Screw(ISO4762); B24='All; C24='-; D24='M5x20-Screw(ISO4762); E24='-; F24='-; +12 more cells
FEATURE [App::Link] P_M3_12_Screw001  label="P_X_Axis_Overlap_Bolt0_Bolt"
  AttachedBy = #LCS_M3_12_Screw
  AttachedTo = P_X_Axis_Base#LCS_X_Axis_Base_Bolt0
  LinkPlacement = pos=(52.8818,-72.7856,46.9994) rot=(0.90714,0.294748,0.300368;1.64928rad)
  LinkedObject = -> <external standard-parts.FCStd>#Part018
  Placement = pos=(52.8818,-72.7856,46.9994) rot=(0.90714,0.294748,0.300368;1.64928rad)
  SolverId = Asm4EE
  expr: Placement = P_X_Axis_Base.Placement * jrobot_x_axis_parts#LCS_X_Axis_Base_Bolt0.Placement * AttachmentOffset * standard_parts#LCS_M3_12_Screw.Placement ^ -1
FEATURE [App::Link] P_M3_X_Axis_Overlap_1  label="P_X_Axis_Overlap_Bolt1_Bolt"
  AttachedBy = #LCS_M3_12_Screw
  AttachedTo = P_X_Axis_Base#LCS_X_Axis_Base_Bolt1
  LinkPlacement = pos=(85.5646,27.8016,46.9994) rot=(0.453526,0.624225,0.636128;2.27573rad)
  LinkedObject = -> <external standard-parts.FCStd>#Part018
  Placement = pos=(85.5646,27.8016,46.9994) rot=(0.453526,0.624225,0.636128;2.27573rad)
  SolverId = Asm4EE
  expr: Placement = P_X_Axis_Base.Placement * jrobot_x_axis_parts#LCS_X_Axis_Base_Bolt1.Placement * AttachmentOffset * standard_parts#LCS_M3_12_Screw.Placement ^ -1
FEATURE [App::Link] P_M3_X_Axis_Overlap_2  label="P_X_Axis_Overlap_Bolt2_Bolt"
  AttachedBy = #LCS_M3_12_Screw
  AttachedTo = P_X_Axis_Base#LCS_X_Axis_Base_Bolt2
  LinkPlacement = pos=(-6.64599e-08,89.9679,46.9994) rot=(0,0.700397,0.713753;3.14159rad)
  LinkedObject = -> <external standard-parts.FCStd>#Part018
  Placement = pos=(-6.64599e-08,89.9679,46.9994) rot=(0,0.700397,0.713753;3.14159rad)
  SolverId = Asm4EE
  expr: Placement = P_X_Axis_Base.Placement * jrobot_x_axis_parts#LCS_X_Axis_Base_Bolt2.Placement * AttachmentOffset * standard_parts#LCS_M3_12_Screw.Placement ^ -1
FEATURE [App::Link] P_M3_X_Axis_Overlap_3  label="P_X_Axis_Overlap_Bolt3_Bolt"
  AttachedBy = #LCS_M3_12_Screw
  AttachedTo = P_X_Axis_Base#LCS_X_Axis_Base_Bolt3
  LinkPlacement = pos=(-85.5646,27.8016,46.9994) rot=(-0.453526,0.624224,0.636128;4.00746rad)
  LinkedObject = -> <external standard-parts.FCStd>#Part018
  Placement = pos=(-85.5646,27.8016,46.9994) rot=(-0.453526,0.624224,0.636128;4.00746rad)
  SolverId = Asm4EE
  expr: Placement = P_X_Axis_Base.Placement * jrobot_x_axis_parts#LCS_X_Axis_Base_Bolt3.Placement * AttachmentOffset * standard_parts#LCS_M3_12_Screw.Placement ^ -1
FEATURE [App::Link] P_M3_X_Axis_Overlap_4  label="P_X_Axis_Overlap_Bolt4_Bolt"
  AttachedBy = #LCS_M3_12_Screw
  AttachedTo = P_X_Axis_Base#LCS_X_Axis_Base_Bolt4
  LinkPlacement = pos=(-52.8818,-72.7856,46.9994) rot=(0.90714,-0.294748,-0.300368;1.64928rad)
  LinkedObject = -> <external standard-parts.FCStd>#Part018
  Placement = pos=(-52.8818,-72.7856,46.9994) rot=(0.90714,-0.294748,-0.300368;1.64928rad)
  SolverId = Asm4EE
  expr: Placement = P_X_Axis_Base.Placement * jrobot_x_axis_parts#LCS_X_Axis_Base_Bolt4.Placement * AttachmentOffset * standard_parts#LCS_M3_12_Screw.Placement ^ -1
FEATURE [App::Link] P_M3_Nut  label="P_X_Axis_Overlap_Bolt0_Nut"
  AttachedBy = #LCS_M3_Nut
  AttachedTo = P_X_Axis_Base#LCS_X_Axis_Base_Bolt0
  AttachmentOffset = pos=(0,0,-8) rot=(0,0,1;0rad)
  LinkPlacement = pos=(48.1804,-66.3146,46.8483) rot=(0.90714,0.294748,0.300368;1.64928rad)
  LinkedObject = -> <external standard-parts.FCStd>#Part024
  Placement = pos=(48.1804,-66.3146,46.8483) rot=(0.90714,0.294748,0.300368;1.64928rad)
  SolverId = Asm4EE
  expr: Placement = P_X_Axis_Base.Placement * jrobot_x_axis_parts#LCS_X_Axis_Base_Bolt0.Placement * AttachmentOffset * standard_parts#LCS_M3_Nut.Placement ^ -1
FEATURE [App::Link] P_M3_X_Axis_Overlap_5  label="P_X_Axis_Overlap_Bolt1_Nut"
  AttachedBy = #LCS_M3_Nut
  AttachedTo = P_X_Axis_Base#LCS_X_Axis_Base_Bolt1
  AttachmentOffset = pos=(0,0,-8) rot=(0,0,1;0rad)
  LinkPlacement = pos=(77.9575,25.3299,46.8483) rot=(0.453526,0.624225,0.636128;2.27573rad)
  LinkedObject = -> <external standard-parts.FCStd>#Part024
  Placement = pos=(77.9575,25.3299,46.8483) rot=(0.453526,0.624225,0.636128;2.27573rad)
  SolverId = Asm4EE
  expr: Placement = P_X_Axis_Base.Placement * jrobot_x_axis_parts#LCS_X_Axis_Base_Bolt1.Placement * AttachmentOffset * standard_parts#LCS_M3_Nut.Placement ^ -1
FEATURE [App::Link] P_M3_X_Axis_Overlap_6  label="P_X_Axis_Overlap_Bolt2_Nut"
  AttachedBy = #LCS_M3_Nut
  AttachedTo = P_X_Axis_Base#LCS_X_Axis_Base_Bolt2
  AttachmentOffset = pos=(0,0,-8) rot=(0,0,1;0rad)
  LinkPlacement = pos=(2.55178e-07,81.9693,46.8483) rot=(0,0.700397,0.713753;3.14159rad)
  LinkedObject = -> <external standard-parts.FCStd>#Part024
  Placement = pos=(2.55178e-07,81.9693,46.8483) rot=(0,0.700397,0.713753;3.14159rad)
  SolverId = Asm4EE
  expr: Placement = P_X_Axis_Base.Placement * jrobot_x_axis_parts#LCS_X_Axis_Base_Bolt2.Placement * AttachmentOffset * standard_parts#LCS_M3_Nut.Placement ^ -1
FEATURE [App::Link] P_M3_X_Axis_Overlap_7  label="P_X_Axis_Overlap_Bolt3_Nut"
  AttachedBy = #LCS_M3_Nut
  AttachedTo = P_X_Axis_Base#LCS_X_Axis_Base_Bolt3
  AttachmentOffset = pos=(0,0,-8) rot=(0,0,1;0rad)
  LinkPlacement = pos=(-77.9575,25.3299,46.8483) rot=(-0.453526,0.624224,0.636128;4.00746rad)
  LinkedObject = -> <external standard-parts.FCStd>#Part024
  Placement = pos=(-77.9575,25.3299,46.8483) rot=(-0.453526,0.624224,0.636128;4.00746rad)
  SolverId = Asm4EE
  expr: Placement = P_X_Axis_Base.Placement * jrobot_x_axis_parts#LCS_X_Axis_Base_Bolt3.Placement * AttachmentOffset * standard_parts#LCS_M3_Nut.Placement ^ -1
FEATURE [App::Link] P_M3_X_Axis_Overlap_8  label="P_X_Axis_Overlap_Bolt4_Nut"
  AttachedBy = #LCS_M3_Nut
  AttachedTo = P_X_Axis_Base#LCS_X_Axis_Base_Bolt4
  AttachmentOffset = pos=(0,0,-8) rot=(0,0,1;0rad)
  LinkPlacement = pos=(-48.1804,-66.3146,46.8483) rot=(0.90714,-0.294748,-0.300368;1.64928rad)
  LinkedObject = -> <external standard-parts.FCStd>#Part024
  Placement = pos=(-48.1804,-66.3146,46.8483) rot=(0.90714,-0.294748,-0.300368;1.64928rad)
  SolverId = Asm4EE
  expr: Placement = P_X_Axis_Base.Placement * jrobot_x_axis_parts#LCS_X_Axis_Base_Bolt4.Placement * AttachmentOffset * standard_parts#LCS_M3_Nut.Placement ^ -1
FEATURE [App::Link] P_M5_20_Screw002  label="P_X_Axis_Base_VerticalBearing_Bolt0_Bolt"
  AttachedBy = #LCS_M5_17_Screw
  AttachedTo = P_X_Axis_Top#LCS_X_Axis_Base_VerticalBearing_Bolt0
  LinkPlacement = pos=(-26.2664,80.8398,77) rot=(0.62896,-0.456966,-0.62896;3.99886rad)
  LinkedObject = -> <external standard-parts.FCStd>#Part029
  Placement = pos=(-26.2664,80.8398,77) rot=(0.62896,-0.456966,-0.62896;3.99886rad)
  SolverId = Asm4EE
  expr: Placement = P_X_Axis_Top.Placement * jrobot_x_axis_parts#LCS_X_Axis_Base_VerticalBearing_Bolt0.Placement * AttachmentOffset * standard_parts#LCS_M5_17_Screw.Placement ^ -1
FEATURE [App::Link] P_M5_16_Screw  label="P_X_Axis_Base_VerticalBearing_Bolt1_Bolt"
  AttachedBy = #LCS_M5_17_Screw
  AttachedTo = P_X_Axis_Top#LCS_X_Axis_Base_VerticalBearing_Bolt1
  LinkPlacement = pos=(-85,2.66e-14,77) rot=(0.707107,0,-0.707107;3.14159rad)
  LinkedObject = -> <external standard-parts.FCStd>#Part029
  Placement = pos=(-85,2.66e-14,77) rot=(0.707107,0,-0.707107;3.14159rad)
  SolverId = Asm4EE
  expr: Placement = P_X_Axis_Top.Placement * jrobot_x_axis_parts#LCS_X_Axis_Base_VerticalBearing_Bolt1.Placement * AttachmentOffset * standard_parts#LCS_M5_17_Screw.Placement ^ -1
FEATURE [App::Link] P_M5_16_Screw_2  label="P_X_Axis_Base_VerticalBearing_Bolt2_Bolt"
  AttachedBy = #LCS_M5_17_Screw
  AttachedTo = P_X_Axis_Top#LCS_X_Axis_Base_VerticalBearing_Bolt2
  LinkPlacement = pos=(-26.2664,-80.8398,77) rot=(0.62896,0.456966,-0.62896;2.28433rad)
  LinkedObject = -> <external standard-parts.FCStd>#Part029
  Placement = pos=(-26.2664,-80.8398,77) rot=(0.62896,0.456966,-0.62896;2.28433rad)
  SolverId = Asm4EE
  expr: Placement = P_X_Axis_Top.Placement * jrobot_x_axis_parts#LCS_X_Axis_Base_VerticalBearing_Bolt2.Placement * AttachmentOffset * standard_parts#LCS_M5_17_Screw.Placement ^ -1
FEATURE [App::Link] P_M5_16_Screw_1  label="P_X_Axis_Base_VerticalBearing_Bolt3_Bolt"
  AttachedBy = #LCS_M5_17_Screw
  AttachedTo = P_X_Axis_Top#LCS_X_Axis_Base_VerticalBearing_Bolt3
  LinkPlacement = pos=(68.7664,-49.9617,77) rot=(0.295242,0.908661,-0.295242;1.66643rad)
  LinkedObject = -> <external standard-parts.FCStd>#Part029
  Placement = pos=(68.7664,-49.9617,77) rot=(0.295242,0.908661,-0.295242;1.66643rad)
  SolverId = Asm4EE
  expr: Placement = P_X_Axis_Top.Placement * jrobot_x_axis_parts#LCS_X_Axis_Base_VerticalBearing_Bolt3.Placement * AttachmentOffset * standard_parts#LCS_M5_17_Screw.Placement ^ -1
FEATURE [App::Link] P_M5_16_Screw_3  label="P_X_Axis_Base_VerticalBearing_Bolt4_Bolt"
  AttachedBy = #LCS_M5_17_Screw
  AttachedTo = P_X_Axis_Top#LCS_X_Axis_Base_VerticalBearing_Bolt4
  LinkPlacement = pos=(68.7664,49.9617,77) rot=(-0.295242,0.908661,0.295242;1.66643rad)
  LinkedObject = -> <external standard-parts.FCStd>#Part029
  Placement = pos=(68.7664,49.9617,77) rot=(-0.295242,0.908661,0.295242;1.66643rad)
  SolverId = Asm4EE
  expr: Placement = P_X_Axis_Top.Placement * jrobot_x_axis_parts#LCS_X_Axis_Base_VerticalBearing_Bolt4.Placement * AttachmentOffset * standard_parts#LCS_M5_17_Screw.Placement ^ -1
FEATURE [App::Link] P_M5_Nut004  label="P_X_Axis_Base_VerticalBearing_Bolt0_Nut"
  AttachedBy = #LCS_M3_Nut001
  AttachedTo = P_X_Axis_Top#LCS_X_Axis_Base_VerticalBearing_Bolt0
  AttachmentOffset = pos=(0,0,-13) rot=(0,0,1;0rad)
  LinkPlacement = pos=(-22.2492,68.4761,77) rot=(0.62896,-0.456966,-0.62896;3.99886rad)
  LinkedObject = -> <external standard-parts.FCStd>#Part037
  Placement = pos=(-22.2492,68.4761,77) rot=(0.62896,-0.456966,-0.62896;3.99886rad)
  SolverId = Asm4EE
  expr: Placement = P_X_Axis_Top.Placement * jrobot_x_axis_parts#LCS_X_Axis_Base_VerticalBearing_Bolt0.Placement * AttachmentOffset * standard_parts#LCS_M3_Nut001.Placement ^ -1
FEATURE [App::Link] P_M5_Nut_3  label="P_X_Axis_Base_VerticalBearing_Bolt1_Nut"
  AttachedBy = #LCS_M3_Nut001
  AttachedTo = P_X_Axis_Top#LCS_X_Axis_Base_VerticalBearing_Bolt1
  AttachmentOffset = pos=(0,0,-13) rot=(0,0,1;0rad)
  LinkPlacement = pos=(-72,2.38e-14,77) rot=(0.707107,0,-0.707107;3.14159rad)
  LinkedObject = -> <external standard-parts.FCStd>#Part037
  Placement = pos=(-72,2.38e-14,77) rot=(0.707107,0,-0.707107;3.14159rad)
  SolverId = Asm4EE
  expr: Placement = P_X_Axis_Top.Placement * jrobot_x_axis_parts#LCS_X_Axis_Base_VerticalBearing_Bolt1.Placement * AttachmentOffset * standard_parts#LCS_M3_Nut001.Placement ^ -1
FEATURE [App::Link] P_M5_Nut_4  label="P_X_Axis_Base_VerticalBearing_Bolt2_Nut"
  AttachedBy = #LCS_M3_Nut001
  AttachedTo = P_X_Axis_Top#LCS_X_Axis_Base_VerticalBearing_Bolt2
  AttachmentOffset = pos=(0,0,-13) rot=(0,0,1;0rad)
  LinkPlacement = pos=(-22.2492,-68.4761,77) rot=(0.62896,0.456966,-0.62896;2.28433rad)
  LinkedObject = -> <external standard-parts.FCStd>#Part037
  Placement = pos=(-22.2492,-68.4761,77) rot=(0.62896,0.456966,-0.62896;2.28433rad)
  SolverId = Asm4EE
  expr: Placement = P_X_Axis_Top.Placement * jrobot_x_axis_parts#LCS_X_Axis_Base_VerticalBearing_Bolt2.Placement * AttachmentOffset * standard_parts#LCS_M3_Nut001.Placement ^ -1
FEATURE [App::Link] P_M5_Nut_5  label="P_X_Axis_Base_VerticalBearing_Bolt3_Nut"
  AttachedBy = #LCS_M3_Nut001
  AttachedTo = P_X_Axis_Top#LCS_X_Axis_Base_VerticalBearing_Bolt3
  AttachmentOffset = pos=(0,0,-13) rot=(0,0,1;0rad)
  LinkPlacement = pos=(58.2492,-42.3205,77) rot=(0.295242,0.908661,-0.295242;1.66643rad)
  LinkedObject = -> <external standard-parts.FCStd>#Part037
  Placement = pos=(58.2492,-42.3205,77) rot=(0.295242,0.908661,-0.295242;1.66643rad)
  SolverId = Asm4EE
  expr: Placement = P_X_Axis_Top.Placement * jrobot_x_axis_parts#LCS_X_Axis_Base_VerticalBearing_Bolt3.Placement * AttachmentOffset * standard_parts#LCS_M3_Nut001.Placement ^ -1
FEATURE [App::Link] P_M5_Nut_6  label="P_X_Axis_Base_VerticalBearing_Bolt4_Nut"
  AttachedBy = #LCS_M3_Nut001
  AttachedTo = P_X_Axis_Top#LCS_X_Axis_Base_VerticalBearing_Bolt4
  AttachmentOffset = pos=(0,0,-13) rot=(0,0,1;0rad)
  LinkPlacement = pos=(58.2492,42.3205,77) rot=(-0.295242,0.908661,0.295242;1.66643rad)
  LinkedObject = -> <external standard-parts.FCStd>#Part037
  Placement = pos=(58.2492,42.3205,77) rot=(-0.295242,0.908661,0.295242;1.66643rad)
  SolverId = Asm4EE
  expr: Placement = P_X_Axis_Top.Placement * jrobot_x_axis_parts#LCS_X_Axis_Base_VerticalBearing_Bolt4.Placement * AttachmentOffset * standard_parts#LCS_M3_Nut001.Placement ^ -1
FEATURE [App::Link] P_M3_Nut001  label="P_X_Axis_LimitSwitch_Hole0_Nut"
  AttachedBy = #LCS_M3_Nut
  AttachedTo = P_X_Axis_Top#LCS_X_Axis_Top_LimitSwitch_0
  AttachmentOffset = pos=(0,0,-7) rot=(0,0,1;0rad)
  LinkPlacement = pos=(9.625,50,75) rot=(0,0,1;1.5708rad)
  LinkedObject = -> <external standard-parts.FCStd>#Part024
  Placement = pos=(9.625,50,75) rot=(0,0,1;1.5708rad)
  SolverId = Asm4EE
  expr: Placement = P_X_Axis_Top.Placement * jrobot_x_axis_parts#LCS_X_Axis_Top_LimitSwitch_0.Placement * AttachmentOffset * standard_parts#LCS_M3_Nut.Placement ^ -1
FEATURE [App::Link] P_M3_Nut_2  label="P_X_Axis_LimitSwitch_Hole1_Nut"
  AttachedBy = #LCS_M3_Nut
  AttachedTo = P_X_Axis_Top#LCS_X_Axis_Top_LimitSwitch_1
  AttachmentOffset = pos=(0,0,-7) rot=(0,0,1;0rad)
  LinkPlacement = pos=(-9.625,50,75) rot=(0,0,1;1.5708rad)
  LinkedObject = -> <external standard-parts.FCStd>#Part024
  Placement = pos=(-9.625,50,75) rot=(0,0,1;1.5708rad)
  SolverId = Asm4EE
  expr: Placement = P_X_Axis_Top.Placement * jrobot_x_axis_parts#LCS_X_Axis_Top_LimitSwitch_1.Placement * AttachmentOffset * standard_parts#LCS_M3_Nut.Placement ^ -1
FEATURE [App::Link] P_M5_50_Screw  label="P_M5_X_Axis_Base_Mount_Bolt0"
  AttachedBy = #LCS_M5_45_Screw001
  AttachedTo = P_X_Axis_Base#LCS_X_Axis_Base_Mount0
  LinkPlacement = pos=(-75,-75,5) rot=(0,0,1;1.5708rad)
  LinkedObject = -> <external standard-parts.FCStd>#Part032
  Placement = pos=(-75,-75,5) rot=(0,0,1;1.5708rad)
  SolverId = Asm4EE
  expr: Placement = P_X_Axis_Base.Placement * jrobot_x_axis_parts#LCS_X_Axis_Base_Mount0.Placement * AttachmentOffset * standard_parts#LCS_M5_45_Screw001.Placement ^ -1
FEATURE [App::Link] P_M5_50_Screw_2  label="P_M5_X_Axis_Base_Mount_Bolt1"
  AttachedBy = #LCS_M5_30_Screw
  AttachedTo = P_X_Axis_Base#LCS_X_Axis_Base_Mount1
  LinkPlacement = pos=(75,-75,5) rot=(0,0,-1;1.5708rad)
  LinkedObject = -> <external standard-parts.FCStd>#Part032
  Placement = pos=(75,-75,5) rot=(0,0,-1;1.5708rad)
  SolverId = Asm4EE
  expr: Placement = P_X_Axis_Base.Placement * jrobot_x_axis_parts#LCS_X_Axis_Base_Mount1.Placement * AttachmentOffset * standard_parts#LCS_M5_30_Screw.Placement ^ -1
FEATURE [App::Link] P_M5_50_Screw_1  label="P_M5_X_Axis_Base_Mount_Bolt2"
  AttachedBy = #LCS_M5_30_Screw
  AttachedTo = P_X_Axis_Base#LCS_X_Axis_Base_Mount2
  LinkPlacement = pos=(75,75,5) rot=(0,0,-1;1.5708rad)
  LinkedObject = -> <external standard-parts.FCStd>#Part032
  Placement = pos=(75,75,5) rot=(0,0,-1;1.5708rad)
  SolverId = Asm4EE
  expr: Placement = P_X_Axis_Base.Placement * jrobot_x_axis_parts#LCS_X_Axis_Base_Mount2.Placement * AttachmentOffset * standard_parts#LCS_M5_30_Screw.Placement ^ -1
FEATURE [App::Link] P_M5_50_Screw_3  label="P_M5_X_Axis_Base_Mount_Bolt3"
  AttachedBy = #LCS_M5_30_Screw
  AttachedTo = P_X_Axis_Base#LCS_X_Axis_Base_Mount3
  LinkPlacement = pos=(-75,75,5) rot=(0,0,1;1.5708rad)
  LinkedObject = -> <external standard-parts.FCStd>#Part032
  Placement = pos=(-75,75,5) rot=(0,0,1;1.5708rad)
  SolverId = Asm4EE
  expr: Placement = P_X_Axis_Base.Placement * jrobot_x_axis_parts#LCS_X_Axis_Base_Mount3.Placement * AttachmentOffset * standard_parts#LCS_M5_30_Screw.Placement ^ -1
FEATURE [App::Link] P_M5_Nut005  label="P_M5_X_Axis_Base_Mount_Nut0"
  AttachedBy = #LCS_M3_Nut001
  AttachedTo = P_X_Axis_Base#LCS_X_Axis_Base_Mount0
  AttachmentOffset = pos=(0,0,-20) rot=(0,0,1;0rad)
  LinkPlacement = pos=(-75,-75,-15) rot=(0,0,1;1.5708rad)
  LinkedObject = -> <external standard-parts.FCStd>#Part037
  Placement = pos=(-75,-75,-15) rot=(0,0,1;1.5708rad)
  SolverId = Asm4EE
  expr: Placement = P_X_Axis_Base.Placement * jrobot_x_axis_parts#LCS_X_Axis_Base_Mount0.Placement * AttachmentOffset * standard_parts#LCS_M3_Nut001.Placement ^ -1
FEATURE [App::Link] P_M5_Nut_7  label="P_M5_X_Axis_Base_Mount_Nut1"
  AttachedBy = #LCS_M3_Nut001
  AttachedTo = P_X_Axis_Base#LCS_X_Axis_Base_Mount1
  AttachmentOffset = pos=(0,0,-20) rot=(0,0,1;0rad)
  LinkPlacement = pos=(75,-75,-15) rot=(0,0,-1;1.5708rad)
  LinkedObject = -> <external standard-parts.FCStd>#Part037
  Placement = pos=(75,-75,-15) rot=(0,0,-1;1.5708rad)
  SolverId = Asm4EE
  expr: Placement = P_X_Axis_Base.Placement * jrobot_x_axis_parts#LCS_X_Axis_Base_Mount1.Placement * AttachmentOffset * standard_parts#LCS_M3_Nut001.Placement ^ -1
FEATURE [App::Link] P_M5_Nut_8  label="P_M5_X_Axis_Base_Mount_Nut2"
  AttachedBy = #LCS_M3_Nut001
  AttachedTo = P_X_Axis_Base#LCS_X_Axis_Base_Mount2
  AttachmentOffset = pos=(0,0,-20) rot=(0,0,1;0rad)
  LinkPlacement = pos=(75,75,-15) rot=(0,0,-1;1.5708rad)
  LinkedObject = -> <external standard-parts.FCStd>#Part037
  Placement = pos=(75,75,-15) rot=(0,0,-1;1.5708rad)
  SolverId = Asm4EE
  expr: Placement = P_X_Axis_Base.Placement * jrobot_x_axis_parts#LCS_X_Axis_Base_Mount2.Placement * AttachmentOffset * standard_parts#LCS_M3_Nut001.Placement ^ -1
FEATURE [App::Link] P_M5_Nut_9  label="P_M5_X_Axis_Base_Mount_Nut3"
  AttachedBy = #LCS_M3_Nut001
  AttachedTo = P_X_Axis_Base#LCS_X_Axis_Base_Mount3
  AttachmentOffset = pos=(0,0,-20) rot=(0,0,1;0rad)
  LinkPlacement = pos=(-75,75,-15) rot=(0,0,1;1.5708rad)
  LinkedObject = -> <external standard-parts.FCStd>#Part037
  Placement = pos=(-75,75,-15) rot=(0,0,1;1.5708rad)
  SolverId = Asm4EE
  expr: Placement = P_X_Axis_Base.Placement * jrobot_x_axis_parts#LCS_X_Axis_Base_Mount3.Placement * AttachmentOffset * standard_parts#LCS_M3_Nut001.Placement ^ -1
FEATURE [App::Link] P_M3_12_Screw002  label="P_M3_X_Axis_MotorMount_Bolt0"
  AttachedBy = #LCS_M3_12_Screw
  AttachedTo = P_X_Axis_MotorMount#LCS_X_Axis_MotorMount_Mount0
  LinkPlacement = pos=(62.2084,69.0894,72.0005) rot=(-0.88065,0.33805,-0.331931;1.71565rad)
  LinkedObject = -> <external standard-parts.FCStd>#Part020
  Placement = pos=(62.2084,69.0894,72.0005) rot=(-0.88065,0.33805,-0.331931;1.71565rad)
  SolverId = Asm4EE
  expr: Placement = P_X_Axis_MotorMount.Placement * jrobot_x_axis_parts#LCS_X_Axis_MotorMount_Mount0.Placement * AttachmentOffset * standard_parts#LCS_M3_12_Screw.Placement ^ -1
FEATURE [App::Link] P_M3_12_Screw_3  label="P_M3_X_Axis_MotorMount_Bolt1"
  AttachedBy = #LCS_M3_16_Screw
  AttachedTo = P_X_Axis_MotorMount#LCS_X_Axis_MotorMount_Mount1
  LinkPlacement = pos=(62.2084,69.0894,62.0005) rot=(-0.88065,0.33805,-0.331931;1.71565rad)
  LinkedObject = -> <external standard-parts.FCStd>#Part020
  Placement = pos=(62.2084,69.0894,62.0005) rot=(-0.88065,0.33805,-0.331931;1.71565rad)
  SolverId = Asm4EE
  expr: Placement = P_X_Axis_MotorMount.Placement * jrobot_x_axis_parts#LCS_X_Axis_MotorMount_Mount1.Placement * AttachmentOffset * standard_parts#LCS_M3_16_Screw.Placement ^ -1
FEATURE [App::Link] P_M3_12_Screw_1  label="P_M3_X_Axis_MotorMount_Bolt2"
  AttachedBy = #LCS_M3_16_Screw
  AttachedTo = P_X_Axis_MotorMount#LCS_X_Axis_MotorMount_Mount2
  LinkPlacement = pos=(-62.2084,69.0894,72.0005) rot=(-0.88065,-0.33805,0.331931;1.71565rad)
  LinkedObject = -> <external standard-parts.FCStd>#Part020
  Placement = pos=(-62.2084,69.0894,72.0005) rot=(-0.88065,-0.33805,0.331931;1.71565rad)
  SolverId = Asm4EE
  expr: Placement = P_X_Axis_MotorMount.Placement * jrobot_x_axis_parts#LCS_X_Axis_MotorMount_Mount2.Placement * AttachmentOffset * standard_parts#LCS_M3_16_Screw.Placement ^ -1
FEATURE [App::Link] P_M3_12_Screw_4  label="P_M3_X_Axis_MotorMount_Bolt3"
  AttachedBy = #LCS_M3_16_Screw
  AttachedTo = P_X_Axis_MotorMount#LCS_X_Axis_MotorMount_Mount3
  LinkPlacement = pos=(-62.2084,69.0894,62.0005) rot=(-0.88065,-0.33805,0.331931;1.71565rad)
  LinkedObject = -> <external standard-parts.FCStd>#Part020
  Placement = pos=(-62.2084,69.0894,62.0005) rot=(-0.88065,-0.33805,0.331931;1.71565rad)
  SolverId = Asm4EE
  expr: Placement = P_X_Axis_MotorMount.Placement * jrobot_x_axis_parts#LCS_X_Axis_MotorMount_Mount3.Placement * AttachmentOffset * standard_parts#LCS_M3_16_Screw.Placement ^ -1
FEATURE [App::Link] P_M3_Nut002  label="P_M3_X_Axis_MotorMount_Nut0"
  AttachedBy = #LCS_M3_Nut
  AttachedTo = P_X_Axis_MotorMount#LCS_X_Axis_MotorMount_Mount0
  AttachmentOffset = pos=(0,0,-12) rot=(0,0,1;0rad)
  LinkPlacement = pos=(54.1801,60.1731,72.2197) rot=(-0.88065,0.33805,-0.331931;1.71565rad)
  LinkedObject = -> <external standard-parts.FCStd>#Part024
  Placement = pos=(54.1801,60.1731,72.2197) rot=(-0.88065,0.33805,-0.331931;1.71565rad)
  SolverId = Asm4EE
  expr: Placement = P_X_Axis_MotorMount.Placement * jrobot_x_axis_parts#LCS_X_Axis_MotorMount_Mount0.Placement * AttachmentOffset * standard_parts#LCS_M3_Nut.Placement ^ -1
FEATURE [App::Link] P_M3_Nut_3  label="P_M3_X_Axis_MotorMount_Nut1"
  AttachedBy = #LCS_M3_Nut
  AttachedTo = P_X_Axis_MotorMount#LCS_X_Axis_MotorMount_Mount1
  AttachmentOffset = pos=(0,0,-12) rot=(0,0,1;0rad)
  LinkPlacement = pos=(54.1801,60.1731,62.2197) rot=(-0.88065,0.33805,-0.331931;1.71565rad)
  LinkedObject = -> <external standard-parts.FCStd>#Part024
  Placement = pos=(54.1801,60.1731,62.2197) rot=(-0.88065,0.33805,-0.331931;1.71565rad)
  SolverId = Asm4EE
  expr: Placement = P_X_Axis_MotorMount.Placement * jrobot_x_axis_parts#LCS_X_Axis_MotorMount_Mount1.Placement * AttachmentOffset * standard_parts#LCS_M3_Nut.Placement ^ -1
FEATURE [App::Link] P_M3_Nut_1  label="P_M3_X_Axis_MotorMount_Nut2"
  AttachedBy = #LCS_M3_Nut
  AttachedTo = P_X_Axis_MotorMount#LCS_X_Axis_MotorMount_Mount2
  AttachmentOffset = pos=(0,0,-12) rot=(0,0,1;0rad)
  LinkPlacement = pos=(-54.1801,60.1731,72.2197) rot=(-0.88065,-0.33805,0.331931;1.71565rad)
  LinkedObject = -> <external standard-parts.FCStd>#Part024
  Placement = pos=(-54.1801,60.1731,72.2197) rot=(-0.88065,-0.33805,0.331931;1.71565rad)
  SolverId = Asm4EE
  expr: Placement = P_X_Axis_MotorMount.Placement * jrobot_x_axis_parts#LCS_X_Axis_MotorMount_Mount2.Placement * AttachmentOffset * standard_parts#LCS_M3_Nut.Placement ^ -1
FEATURE [App::Link] P_M3_Nut_4  label="P_M3_X_Axis_MotorMount_Nut3"
  AttachedBy = #LCS_M3_Nut
  AttachedTo = P_X_Axis_MotorMount#LCS_X_Axis_MotorMount_Mount3
  AttachmentOffset = pos=(0,0,-12) rot=(0,0,1;0rad)
  LinkPlacement = pos=(-54.1801,60.1731,62.2197) rot=(-0.88065,-0.33805,0.331931;1.71565rad)
  LinkedObject = -> <external standard-parts.FCStd>#Part024
  Placement = pos=(-54.1801,60.1731,62.2197) rot=(-0.88065,-0.33805,0.331931;1.71565rad)
  SolverId = Asm4EE
  expr: Placement = P_X_Axis_MotorMount.Placement * jrobot_x_axis_parts#LCS_X_Axis_MotorMount_Mount3.Placement * AttachmentOffset * standard_parts#LCS_M3_Nut.Placement ^ -1
FEATURE [App::DocumentObjectGroup] X_Axis_Assembly
  Group = -> [P_X_Axis_Top,P_Bearing_5mm_16mm_5mm,P_Bearing_5mm_16mm_5mm001,P_Bearing_5mm_16mm_1,P_Bearing_5mm_16mm_2,P_Bearing_5mm_16mm_3,P_Bearing_5mm_16mm_4,P_Bearing_5mm_16mm_5mm002,P_X_Axis_Base,P_Robot_X_Axis_Base_BearingCap,P_LimitSwitch,P_X_Axis_MotorMount,P_Nema23_76mm,P_X_Axis_Belt,P_X_Axis_Rotor,P_X_Axis_BeltTensioner,P_Belt_Idler_GT2_10mm_5mm,P_Belt_Idler_GT2_10mm_5mm_2,P_X_Axis_Shaft,P_M3_16_Screw,+54 more]
FEATURE [App::Link] P_M3_Nut003  label="P_M3_X_Axis_BeltTensioner_Bolt0_Nut"
  AttachedBy = #LCS_M3_Nut
  AttachedTo = P_X_Axis_BeltTensioner#LCS_X_Axis_BeltTensioner_Bolt0
  AttachmentOffset = pos=(0,0,-8) rot=(0,0,1;0rad)
  LinkPlacement = pos=(42.5,123.5,75) rot=(0,0,1;4.71239rad)
  LinkedObject = -> <external standard-parts.FCStd>#Part024
  Placement = pos=(42.5,123.5,75) rot=(0,0,1;4.71239rad)
  SolverId = Asm4EE
  expr: Placement = P_X_Axis_BeltTensioner.Placement * jrobot_x_axis_parts#LCS_X_Axis_BeltTensioner_Bolt0.Placement * AttachmentOffset * standard_parts#LCS_M3_Nut.Placement ^ -1
FEATURE [App::Link] P_M3_Nut_5  label="P_M3_X_Axis_BeltTensioner_Bolt1_Nut"
  AttachedBy = #LCS_M3_Nut
  AttachedTo = P_X_Axis_BeltTensioner#LCS_X_Axis_BeltTensioner_Bolt1
  AttachmentOffset = pos=(0,0,-8) rot=(0,0,1;0rad)
  LinkPlacement = pos=(-42.5,123.5,75) rot=(0,0,1;4.71239rad)
  LinkedObject = -> <external standard-parts.FCStd>#Part024
  Placement = pos=(-42.5,123.5,75) rot=(0,0,1;4.71239rad)
  SolverId = Asm4EE
  expr: Placement = P_X_Axis_BeltTensioner.Placement * jrobot_x_axis_parts#LCS_X_Axis_BeltTensioner_Bolt1.Placement * AttachmentOffset * standard_parts#LCS_M3_Nut.Placement ^ -1
FEATURE [App::Part] Assembly
  AssemblyType = Part::Link
  DrawingName = jrobot-x-axis-assembly.FCStd
  Group = -> [LCS_Origin,Constraints,Variables,Configurations,X_Axis_Assembly,P_X_Axis_Top,P_Bearing_5mm_16mm_5mm,P_Bearing_5mm_16mm_5mm001,P_Bearing_5mm_16mm_1,P_Bearing_5mm_16mm_2,P_Bearing_5mm_16mm_3,P_Bearing_5mm_16mm_4,P_Bearing_5mm_16mm_5mm002,P_X_Axis_Base,P_Robot_X_Axis_Base_BearingCap,P_LimitSwitch,P_X_Axis_MotorMount,P_Nema23_76mm,P_X_Axis_Belt,P_X_Axis_Rotor,P_X_Axis_BeltTensioner,+60 more]
  Origin = -> Origin
  PartID = jrobot-x-axis-assembly
  Type = Assembly

RESOLVED EXTERNAL PARTS (link-assembly join: the EXTERNAL_REF files above that resolve inside this repo's crawl, each included once):
---- part jrobot-x-axis-parts.FCStd = doc fcstd_4231072843c4 (96222 chars; too large to inline — full recipe in that document) ----
---- part standard-parts.FCStd = doc fcstd_9b47ef122aeb (208734 chars; too large to inline — full recipe in that document) ----
